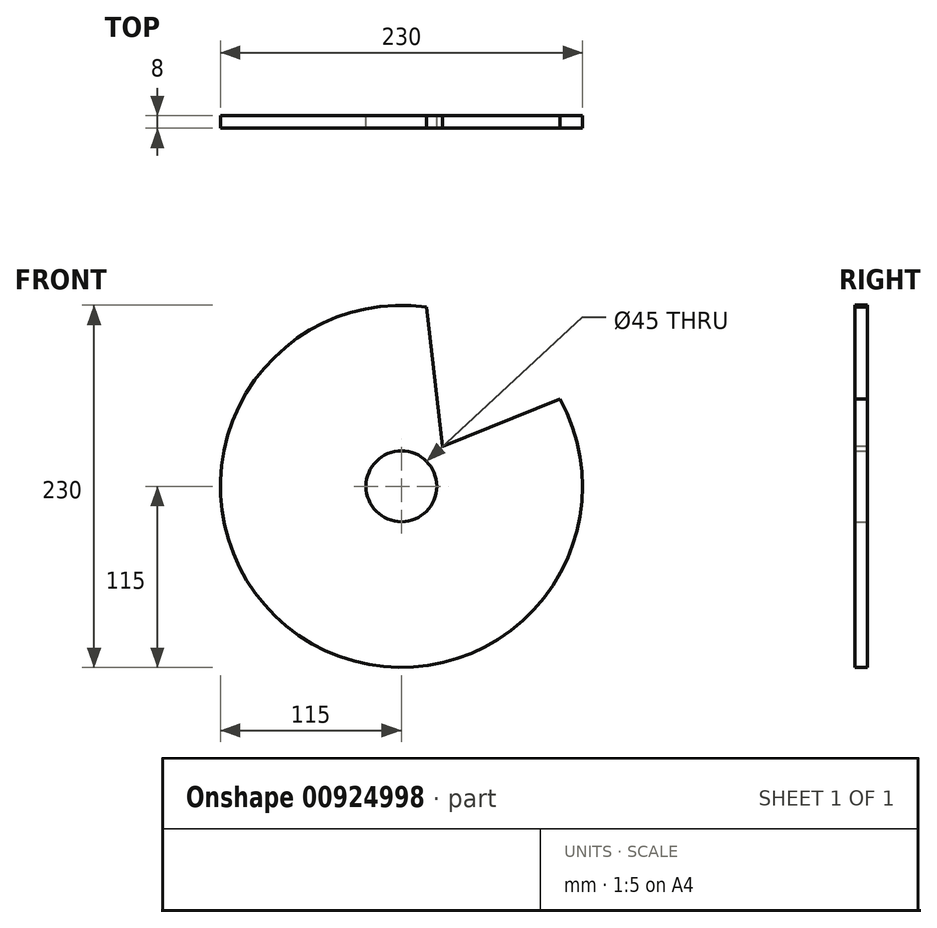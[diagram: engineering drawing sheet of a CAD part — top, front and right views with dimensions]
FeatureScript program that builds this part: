
annotation { "Feature Type Name" : "Feature", "Feature Type Description" : "" }
export const myFeature = defineFeature(function(context is Context, id is Id, definition is map)
    precondition{}
    {
        {
            var Q0;
            Q0=qCreatedBy(makeId("Front.planeOp"),FACE);
            var sketch = newSketch(context, id + "F0", { "sketchPlane" : qUnion([Q0])});
            skCircle(sketch, "E0", {"center": v(0, 0) * mm, "radius": 115 * mm});
            skCircle(sketch, "E1", {"center": v(0, 0) * mm, "radius": 22.5 * mm});
            skSolve(sketch);
        }
        {
            var Q0;
            Q0=makeQuery(id+"F0.imprint","IMPRINT",FACE,{"disambiguationData":[TD([[makeQuery(id+"F0.imprint","IMPRINT",EDGE,{"derivedFrom":sQuery(id+"F0.wireOp",EDGE,"E0")}),1.0]])]});
            extrude(context, id + "F1", {"entities" : qUnion([Q0]), "depth" : 8 * mm, "offsetDistance" : 25 * mm});
        }
        {
            var Q0;
            Q0=makeQuery(id+"F1.opExtrude","CAP_FACE",FACE,{"disambiguationData":[OSD([sQuery(id+"F0.wireOp",EDGE,"E0"),sQuery(id+"F0.wireOp",EDGE,"E1")])],"isStart":false});
            var sketch = newSketch(context, id + "F2", { "sketchPlane" : qUnion([Q0])});
            skLineSegment(sketch, "E2", {"start": v(15.83, 113.9) * mm, "end": v(26.15, 25.23) * mm});
            skLineSegment(sketch, "E3", {"start": v(26.15, 25.23) * mm, "end": v(100.76, 55.42) * mm});
            skLineSegment(sketch, "E4", {"start": v(100.76, 55.42) * mm, "end": v(100.76, 144.04) * mm});
            skLineSegment(sketch, "E5", {"start": v(100.76, 144.04) * mm, "end": v(15.83, 113.9) * mm});
            skSolve(sketch);
        }
        {
            var Q0;
            Q0 = qSketchRegion(id + "F2", true);
            extrude(context, id + "F3", {"entities" : qUnion([Q0]), "operationType" : NewBodyOperationType.REMOVE, "oppositeDirection" : true, "depth" : 25 * mm, "offsetDistance" : 25 * mm});
        }
    });
